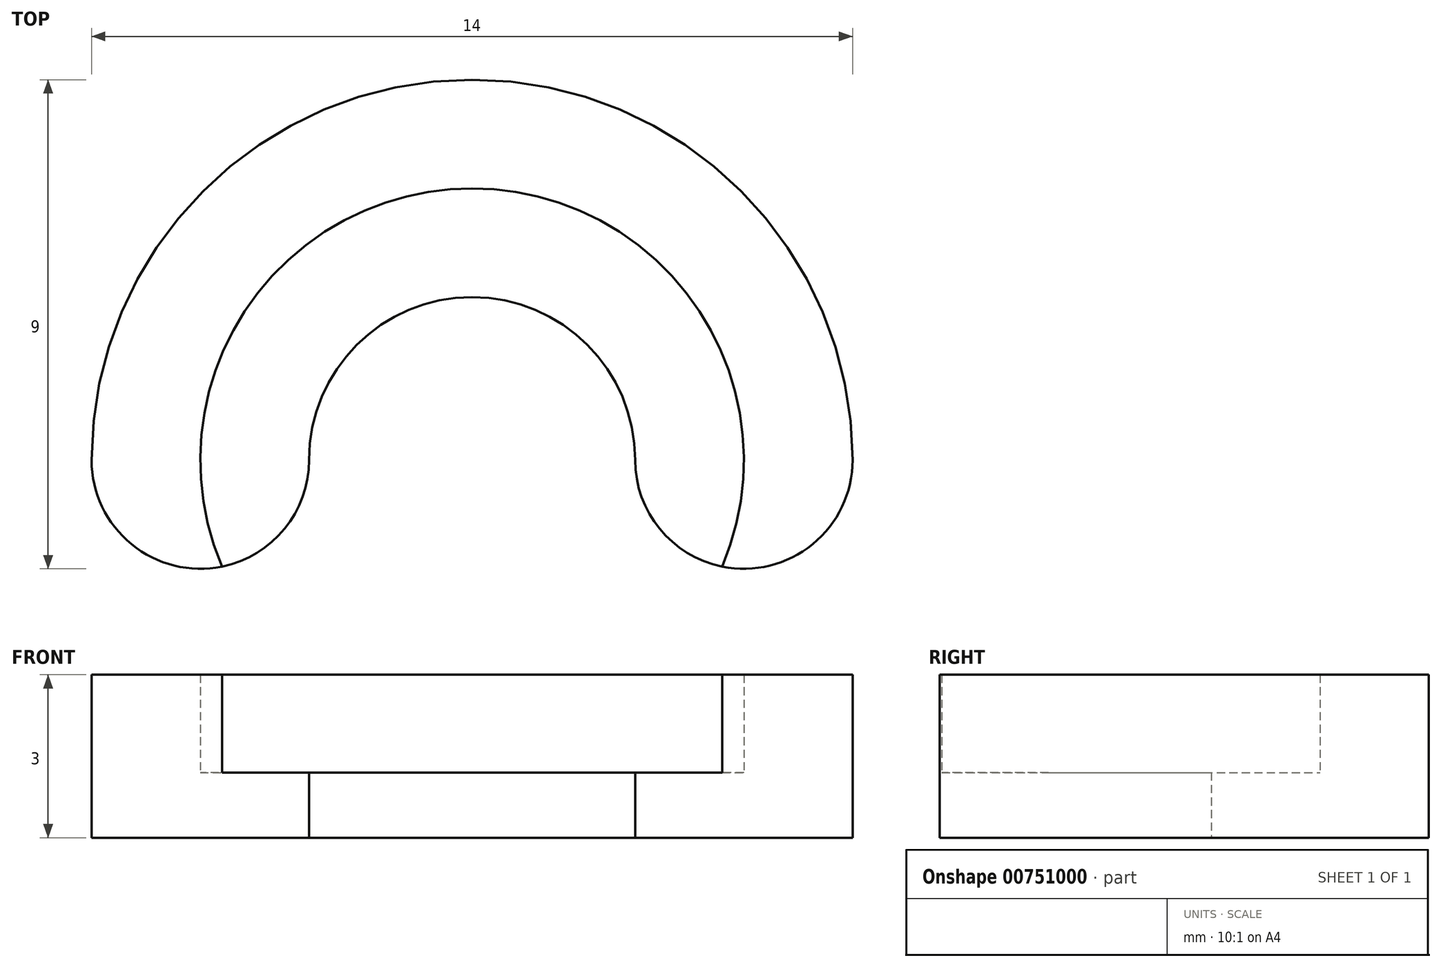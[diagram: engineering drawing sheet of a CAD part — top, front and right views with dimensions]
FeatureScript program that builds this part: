
annotation { "Feature Type Name" : "Feature", "Feature Type Description" : "" }
export const myFeature = defineFeature(function(context is Context, id is Id, definition is map)
    precondition{}
    {
        {
            var Q0;
            Q0=qCreatedBy(makeId("Top.planeOp"),FACE);
            var sketch = newSketch(context, id + "F0", { "sketchPlane" : qUnion([Q0])});
            skCircle(sketch, "E0", {"center": v(0, 0) * mm, "radius": 5 * mm});
            skCircle(sketch, "E1.0", {"center": v(0, 0) * mm, "radius": 3 * mm});
            skCircle(sketch, "E2.0", {"center": v(0, 0) * mm, "radius": 7 * mm});
            skLineSegment(sketch, "E3", {"start": v(0, 0) * mm, "end": v(7, 0) * mm});
            skLineSegment(sketch, "E4", {"start": v(0, 0) * mm, "end": v(-7, 0) * mm});
            skPoint(sketch, "E5", {"position": v(5, 0) * mm});
            skPoint(sketch, "E6", {"position": v(3, 0) * mm});
            skPoint(sketch, "E7", {"position": v(-3, 0) * mm});
            skPoint(sketch, "E8", {"position": v(-5, 0) * mm});
            skLineSegment(sketch, "E9", {"start": v(0, 0) * mm, "end": v(0, -7) * mm, "construction": true});
            skArc(sketch, "E10", {"start": v(-7, 0) * mm, "mid": v(-5, -2) * mm, "end": v(-3, 0) * mm});
            skArc(sketch, "E11.MirrorCS", {"start": v(7, 0) * mm, "mid": v(5, -2) * mm, "end": v(3, 0) * mm});
            skSolve(sketch);
        }
        {
            var Q0;
            {var subQ0=sQuery(id+"F0.wireOp",EDGE,"E4");var subQ1=sQuery(id+"F0.wireOp",EDGE,"E0");var subQ2=makeQuery(id+"F0.imprint","INTERSECT",VERTEX,{"derivedFrom":[subQ1,subQ0]});Q0=makeQuery(id+"F0.imprint","IMPRINT",FACE,{"disambiguationData":[TD([[makeQuery(id+"F0.imprint","IMPRINT",EDGE,{"disambiguationData":[TD([[subQ2,1.0]])],"derivedFrom":subQ1}),1.0]])]});}
            var Q1;
            {var subQ0=sQuery(id+"F0.wireOp",EDGE,"E3");var subQ1=sQuery(id+"F0.wireOp",EDGE,"E0");var subQ2=makeQuery(id+"F0.imprint","INTERSECT",VERTEX,{"derivedFrom":[subQ1,subQ0]});Q1=makeQuery(id+"F0.imprint","IMPRINT",FACE,{"disambiguationData":[TD([[makeQuery(id+"F0.imprint","IMPRINT",EDGE,{"disambiguationData":[TD([[subQ2,1.0]])],"derivedFrom":subQ1}),1.0]])]});}
            var Q2;
            {var subQ0=sQuery(id+"F0.wireOp",EDGE,"E4");var subQ1=sQuery(id+"F0.wireOp",EDGE,"E0");var subQ2=makeQuery(id+"F0.imprint","INTERSECT",VERTEX,{"derivedFrom":[subQ1,subQ0]});Q2=makeQuery(id+"F0.imprint","IMPRINT",FACE,{"disambiguationData":[TD([[makeQuery(id+"F0.imprint","IMPRINT",EDGE,{"disambiguationData":[TD([[subQ2,-1.0]])],"derivedFrom":subQ1}),1.0]])]});}
            extrude(context, id + "F1", {"entities" : qUnion([Q0, Q1, Q2]), "flatOperationType" : FlatOperationType.REMOVE, "depth" : 1.2 * mm, "offsetDistance" : 25 * mm, "domain" : OperationDomain.MODEL});
        }
        {
            var Q0;
            {var subQ0=sQuery(id+"F0.wireOp",EDGE,"E4");var subQ1=sQuery(id+"F0.wireOp",EDGE,"E0");var subQ2=makeQuery(id+"F0.imprint","INTERSECT",VERTEX,{"derivedFrom":[subQ1,subQ0]});Q0=makeQuery(id+"F0.imprint","IMPRINT",FACE,{"disambiguationData":[TD([[makeQuery(id+"F0.imprint","IMPRINT",EDGE,{"disambiguationData":[TD([[subQ2,1.0]])],"derivedFrom":subQ1}),-1.0]])]});}
            var Q1;
            {var subQ0=sQuery(id+"F0.wireOp",EDGE,"E3");var subQ1=sQuery(id+"F0.wireOp",EDGE,"E0");var subQ2=makeQuery(id+"F0.imprint","INTERSECT",VERTEX,{"derivedFrom":[subQ1,subQ0]});Q1=makeQuery(id+"F0.imprint","IMPRINT",FACE,{"disambiguationData":[TD([[makeQuery(id+"F0.imprint","IMPRINT",EDGE,{"disambiguationData":[TD([[subQ2,1.0]])],"derivedFrom":subQ1}),-1.0]])]});}
            var Q2;
            {var subQ0=sQuery(id+"F0.wireOp",EDGE,"E4");var subQ1=sQuery(id+"F0.wireOp",EDGE,"E0");var subQ2=makeQuery(id+"F0.imprint","INTERSECT",VERTEX,{"derivedFrom":[subQ1,subQ0]});Q2=makeQuery(id+"F0.imprint","IMPRINT",FACE,{"disambiguationData":[TD([[makeQuery(id+"F0.imprint","IMPRINT",EDGE,{"disambiguationData":[TD([[subQ2,-1.0]])],"derivedFrom":subQ1}),-1.0]])]});}
            extrude(context, id + "F2", {"entities" : qUnion([Q0, Q1, Q2]), "operationType" : NewBodyOperationType.ADD, "flatOperationType" : FlatOperationType.REMOVE, "depth" : 3 * mm, "offsetDistance" : 25 * mm, "domain" : OperationDomain.MODEL});
        }
    });
